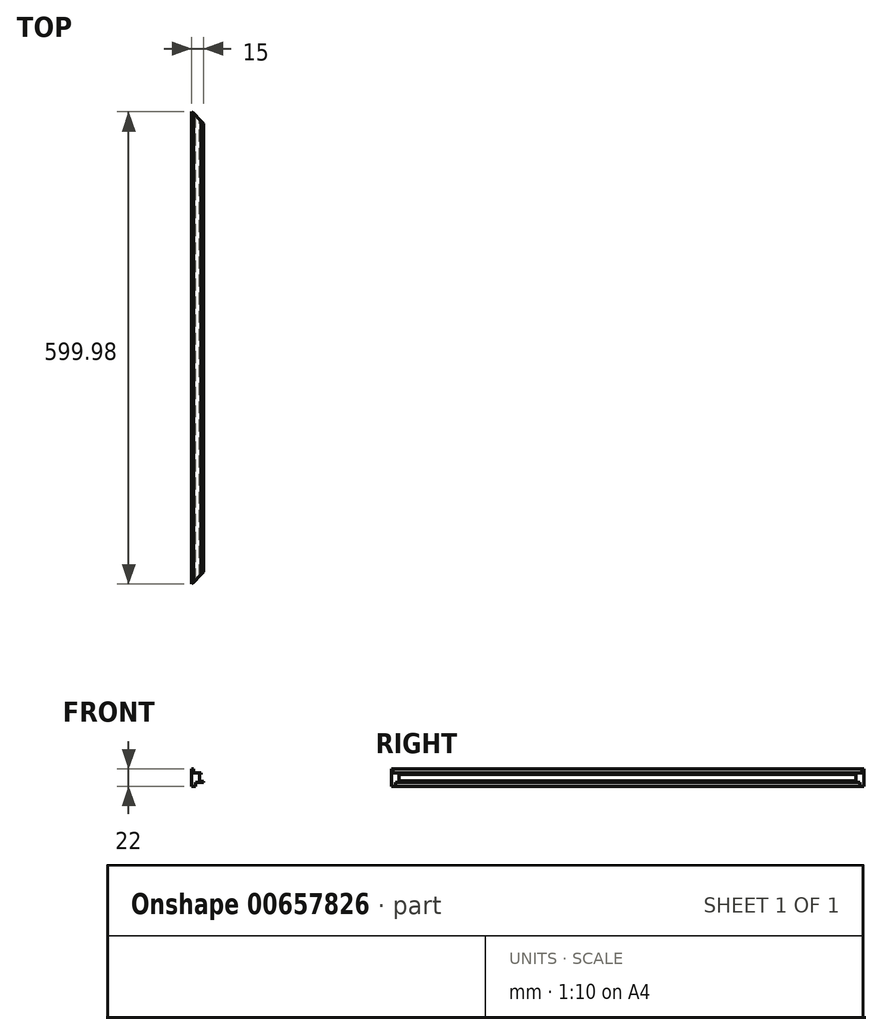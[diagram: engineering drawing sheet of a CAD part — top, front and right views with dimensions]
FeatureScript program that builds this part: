
annotation { "Feature Type Name" : "Feature", "Feature Type Description" : "" }
export const myFeature = defineFeature(function(context is Context, id is Id, definition is map)
    precondition{}
    {
        {
            var Q0;
            Q0=qCreatedBy(makeId("Front.planeOp"),FACE);
            var sketch = newSketch(context, id + "F0", { "sketchPlane" : qUnion([Q0])});
            skLineSegment(sketch, "E0.bottom", {"start": v(0, 0) * mm, "end": v(-10, 0) * mm});
            skLineSegment(sketch, "E0.top", {"start": v(0, -10) * mm, "end": v(-10, -10) * mm});
            skLineSegment(sketch, "E0.left", {"start": v(0, 0) * mm, "end": v(0, -10) * mm});
            skLineSegment(sketch, "E0.right", {"start": v(-10, 0) * mm, "end": v(-10, -10) * mm});
            skLineSegment(sketch, "E1.bottom", {"start": v(0, -10) * mm, "end": v(2.1, -10) * mm});
            skLineSegment(sketch, "E1.top", {"start": v(0, -8.1) * mm, "end": v(2.1, -8.1) * mm});
            skLineSegment(sketch, "E1.left", {"start": v(0, -10) * mm, "end": v(0, -8.1) * mm});
            skLineSegment(sketch, "E1.right", {"start": v(2.1, -10) * mm, "end": v(2.1, -8.1) * mm});
            skLineSegment(sketch, "E2.bottom", {"start": v(2.1, -10) * mm, "end": v(5, -10) * mm});
            skLineSegment(sketch, "E2.top", {"start": v(2.1, -8.7) * mm, "end": v(5, -8.7) * mm});
            skLineSegment(sketch, "E2.left", {"start": v(2.1, -10) * mm, "end": v(2.1, -8.7) * mm});
            skLineSegment(sketch, "E2.right", {"start": v(5, -10) * mm, "end": v(5, -8.7) * mm});
            skLineSegment(sketch, "E3.bottom", {"start": v(-10, 0) * mm, "end": v(2.1, 0) * mm});
            skLineSegment(sketch, "E3.top", {"start": v(-10, 2) * mm, "end": v(2.1, 2) * mm});
            skLineSegment(sketch, "E3.left", {"start": v(-10, 0) * mm, "end": v(-10, 2) * mm});
            skLineSegment(sketch, "E3.right", {"start": v(2.1, 0) * mm, "end": v(2.1, 2) * mm});
            skLineSegment(sketch, "E4.bottom", {"start": v(-10, 2) * mm, "end": v(-8, 2) * mm});
            skLineSegment(sketch, "E4.top", {"start": v(-10, 7) * mm, "end": v(-8, 7) * mm});
            skLineSegment(sketch, "E4.left", {"start": v(-10, 2) * mm, "end": v(-10, 7) * mm});
            skLineSegment(sketch, "E4.right", {"start": v(-8, 2) * mm, "end": v(-8, 7) * mm});
            skLineSegment(sketch, "E5.bottom", {"start": v(-10, -10) * mm, "end": v(-5, -10) * mm});
            skLineSegment(sketch, "E5.top", {"start": v(-10, -15) * mm, "end": v(-5, -15) * mm});
            skLineSegment(sketch, "E5.left", {"start": v(-10, -10) * mm, "end": v(-10, -15) * mm});
            skLineSegment(sketch, "E5.right", {"start": v(-5, -10) * mm, "end": v(-5, -15) * mm});
            skSolve(sketch);
        }
        {
            var Q0;
            Q0 = qSketchRegion(id + "F0", true);
            extrude(context, id + "F1", {"entities" : qUnion([Q0]), "endBound" : BoundingType.SYMMETRIC, "depth" : 300 * mm, "offsetDistance" : 25 * mm});
        }
        {
            var Q0;
            Q0=qCreatedBy(makeId("Top.planeOp"),FACE);
            var sketch = newSketch(context, id + "F2", { "sketchPlane" : qUnion([Q0])});
            skLineSegment(sketch, "E6", {"start": v(-10, -150) * mm, "end": v(5, -150) * mm});
            skLineSegment(sketch, "E7", {"start": v(5, -150) * mm, "end": v(5, -135) * mm});
            skLineSegment(sketch, "E8", {"start": v(-10, -150) * mm, "end": v(5, -135) * mm});
            skSolve(sketch);
        }
        {
            var Q0;
            Q0 = qSketchRegion(id + "F2", true);
            extrude(context, id + "F3", {"entities" : qUnion([Q0]), "operationType" : NewBodyOperationType.REMOVE, "endBound" : BoundingType.SYMMETRIC, "oppositeDirection" : true, "depth" : 100 * mm, "offsetDistance" : 25 * mm});
        }
        {
            var Q0;
            Q0=makeQuery(id+"F1.opExtrude","SWEPT_BODY",BODY,{"disambiguationData":[OSD([sQuery(id+"F0.wireOp",EDGE,"E0.top"),sQuery(id+"F0.wireOp",EDGE,"E0.left"),sQuery(id+"F0.wireOp",EDGE,"E0.right"),sQuery(id+"F0.wireOp",EDGE,"E1.bottom"),sQuery(id+"F0.wireOp",EDGE,"E1.top"),sQuery(id+"F0.wireOp",EDGE,"E1.right"),sQuery(id+"F0.wireOp",EDGE,"E2.bottom"),sQuery(id+"F0.wireOp",EDGE,"E2.top"),sQuery(id+"F0.wireOp",EDGE,"E2.right"),sQuery(id+"F0.wireOp",EDGE,"E3.bottom"),sQuery(id+"F0.wireOp",EDGE,"E3.top"),sQuery(id+"F0.wireOp",EDGE,"E3.left"),sQuery(id+"F0.wireOp",EDGE,"E3.right"),sQuery(id+"F0.wireOp",EDGE,"E4.top"),sQuery(id+"F0.wireOp",EDGE,"E4.left"),sQuery(id+"F0.wireOp",EDGE,"E4.right"),sQuery(id+"F0.wireOp",EDGE,"E5.top"),sQuery(id+"F0.wireOp",EDGE,"E5.left"),sQuery(id+"F0.wireOp",EDGE,"E5.right")])]});
            var Q1;
            Q1=makeQuery(id+"F1.opExtrude","CAP_FACE",FACE,{"disambiguationData":[OSD([sQuery(id+"F0.wireOp",EDGE,"E0.top"),sQuery(id+"F0.wireOp",EDGE,"E0.left"),sQuery(id+"F0.wireOp",EDGE,"E0.right"),sQuery(id+"F0.wireOp",EDGE,"E1.bottom"),sQuery(id+"F0.wireOp",EDGE,"E1.top"),sQuery(id+"F0.wireOp",EDGE,"E1.right"),sQuery(id+"F0.wireOp",EDGE,"E2.bottom"),sQuery(id+"F0.wireOp",EDGE,"E2.top"),sQuery(id+"F0.wireOp",EDGE,"E2.right"),sQuery(id+"F0.wireOp",EDGE,"E3.bottom"),sQuery(id+"F0.wireOp",EDGE,"E3.top"),sQuery(id+"F0.wireOp",EDGE,"E3.left"),sQuery(id+"F0.wireOp",EDGE,"E3.right"),sQuery(id+"F0.wireOp",EDGE,"E4.top"),sQuery(id+"F0.wireOp",EDGE,"E4.left"),sQuery(id+"F0.wireOp",EDGE,"E4.right"),sQuery(id+"F0.wireOp",EDGE,"E5.top"),sQuery(id+"F0.wireOp",EDGE,"E5.left"),sQuery(id+"F0.wireOp",EDGE,"E5.right")])],"isStart":true});
            mirror(context, id + "F4", {"operationType" : NewBodyOperationType.ADD, "entities" : qUnion([Q0]), "mirrorPlane" : qUnion([Q1])});
        }
    });
